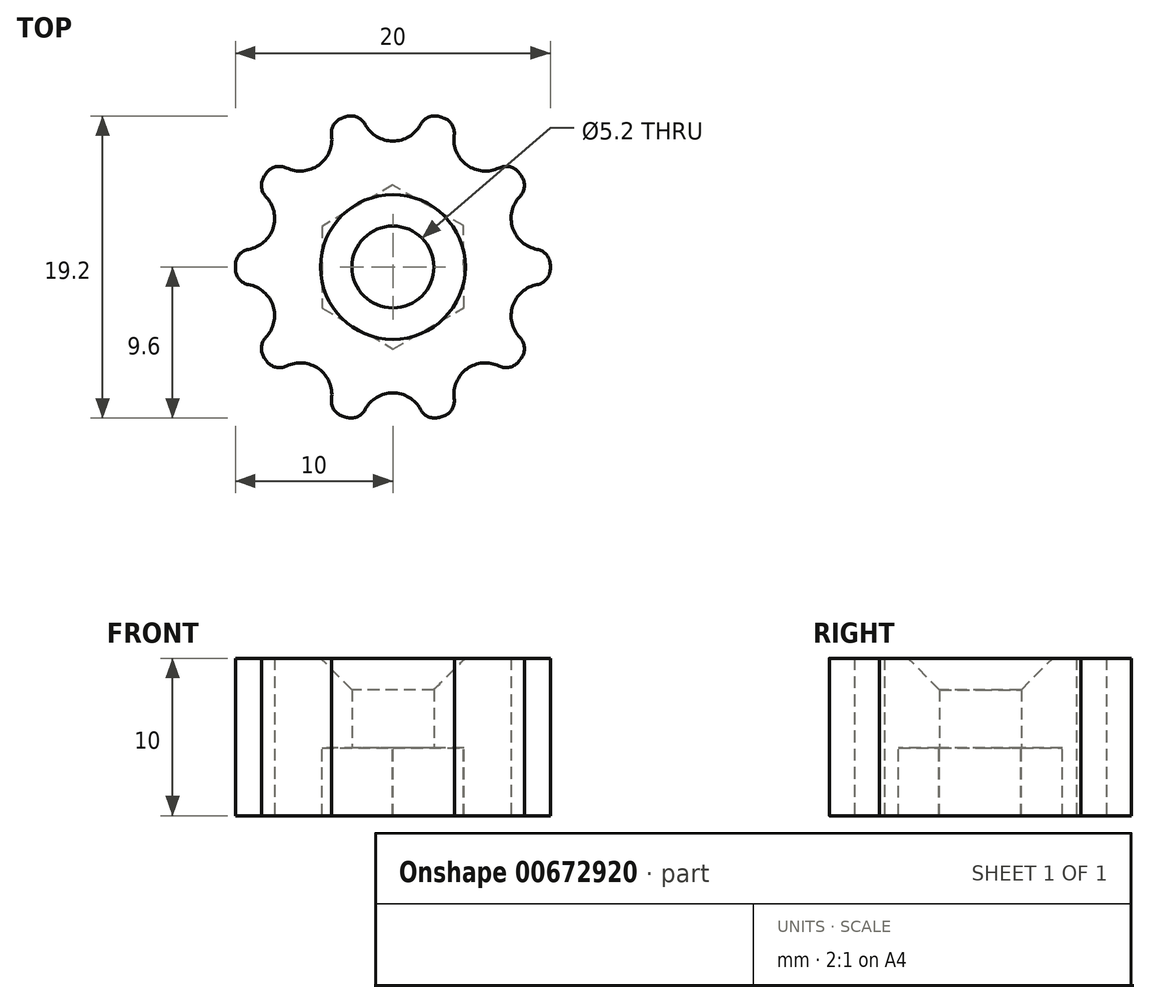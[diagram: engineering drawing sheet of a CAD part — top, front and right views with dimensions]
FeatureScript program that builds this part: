
annotation { "Feature Type Name" : "Feature", "Feature Type Description" : "" }
export const myFeature = defineFeature(function(context is Context, id is Id, definition is map)
    precondition{}
    {
        {
            var Q0;
            Q0=qCreatedBy(makeId("Top.planeOp"),FACE);
            var sketch = newSketch(context, id + "F0", { "sketchPlane" : qUnion([Q0])});
            skCircle(sketch, "E0", {"center": v(0, 0) * mm, "radius": 10 * mm});
            skCircle(sketch, "E1", {"center": v(0, 10) * mm, "radius": 2 * mm});
            skCircle(sketch, "E2.1.0", {"center": v(-5.88, 8.1) * mm, "radius": 2 * mm});
            skCircle(sketch, "E2.2.0", {"center": v(-9.51, 3.1) * mm, "radius": 2 * mm});
            skCircle(sketch, "E2.3.0", {"center": v(-9.51, -3.1) * mm, "radius": 2 * mm});
            skCircle(sketch, "E2.4.0", {"center": v(-5.88, -8.1) * mm, "radius": 2 * mm});
            skCircle(sketch, "E2.5.0", {"center": v(0, -10) * mm, "radius": 2 * mm});
            skCircle(sketch, "E2.6.0", {"center": v(5.88, -8.1) * mm, "radius": 2 * mm});
            skCircle(sketch, "E2.7.0", {"center": v(9.51, -3.1) * mm, "radius": 2 * mm});
            skCircle(sketch, "E2.8.0", {"center": v(9.51, 3.1) * mm, "radius": 2 * mm});
            skCircle(sketch, "E2.9.0", {"center": v(5.88, 8.1) * mm, "radius": 2 * mm});
            skCircle(sketch, "E3", {"center": v(0, 0) * mm, "radius": 2.6 * mm});
            skSolve(sketch);
        }
        {
            var Q0;
            {var subQ0=sQuery(id+"F0.wireOp",EDGE,"E2.8.0");var subQ1=sQuery(id+"F0.wireOp",EDGE,"E0");var subQ17=makeQuery(id+"F0.imprint","INTERSECT",VERTEX,{"disambiguationData":[OD(0.0)],"derivedFrom":[subQ1,subQ0]});Q0=makeQuery(id+"F0.imprint","IMPRINT",FACE,{"disambiguationData":[TD([[makeQuery(id+"F0.imprint","IMPRINT",EDGE,{"disambiguationData":[TD([[subQ17,-1.0]])],"derivedFrom":subQ1}),1.0]])]});}
            extrude(context, id + "F1", {"entities" : qUnion([Q0]), "depth" : 5.7 * mm, "offsetDistance" : 25 * mm});
        }
        {
            var Q0;
            Q0=makeQuery(id+"F1.opExtrude","CAP_EDGE",EDGE,{"disambiguationData":[OSD([sQuery(id+"F0.wireOp",EDGE,"E3")])],"isStart":false});
            chamfer(context, id + "F2", {"entities" : qUnion([Q0]), "width" : 2 * mm, "tangentPropagation" : true});
        }
        {
            var Q0;
            Q0=makeQuery(id+"F1.opExtrude","CAP_FACE",FACE,{"disambiguationData":[OSD([sQuery(id+"F0.wireOp",EDGE,"E0"),sQuery(id+"F0.wireOp",EDGE,"E1"),sQuery(id+"F0.wireOp",EDGE,"E2.1.0"),sQuery(id+"F0.wireOp",EDGE,"E2.2.0"),sQuery(id+"F0.wireOp",EDGE,"E2.3.0"),sQuery(id+"F0.wireOp",EDGE,"E2.4.0"),sQuery(id+"F0.wireOp",EDGE,"E2.5.0"),sQuery(id+"F0.wireOp",EDGE,"E2.6.0"),sQuery(id+"F0.wireOp",EDGE,"E2.7.0"),sQuery(id+"F0.wireOp",EDGE,"E2.8.0"),sQuery(id+"F0.wireOp",EDGE,"E2.9.0"),sQuery(id+"F0.wireOp",EDGE,"E3")])],"isStart":true});
            var sketch = newSketch(context, id + "F3", { "sketchPlane" : qUnion([Q0])});
            skCircle(sketch, "E4.cCircle", {"center": v(0, 0) * mm, "radius": 4.5 * mm, "construction": true});
            skLineSegment(sketch, "E4.0", {"start": v(-4.5, 2.62) * mm, "end": v(0.02, 5.2) * mm});
            skLineSegment(sketch, "E4.1", {"start": v(0.02, 5.2) * mm, "end": v(4.51, 2.58) * mm});
            skLineSegment(sketch, "E4.2", {"start": v(4.51, 2.58) * mm, "end": v(4.5, -2.62) * mm});
            skLineSegment(sketch, "E4.3", {"start": v(4.5, -2.62) * mm, "end": v(-0.02, -5.2) * mm});
            skLineSegment(sketch, "E4.4", {"start": v(-0.02, -5.2) * mm, "end": v(-4.51, -2.58) * mm});
            skLineSegment(sketch, "E4.5", {"start": v(-4.51, -2.58) * mm, "end": v(-4.5, 2.62) * mm});
            skPoint(sketch, "E4.0.midPoint", {"position": v(-2.24, 3.9) * mm});
            skSolve(sketch);
        }
        {
            var Q0;
            Q0=makeQuery(id+"F3.imprint","IMPRINT",FACE,{"disambiguationData":[TD([[makeQuery(id+"F3.imprint","IMPRINT",EDGE,{"derivedFrom":sQuery(id+"F3.wireOp",EDGE,"E4.0")}),1.0]])]});
            extrude(context, id + "F4", {"entities" : qUnion([Q0]), "operationType" : NewBodyOperationType.ADD, "depth" : 4.3 * mm, "offsetDistance" : 25 * mm});
        }
        {
            var Q0;
            {var subQ0=sQuery(id+"F0.wireOp",EDGE,"E2.7.0");var subQ1=sQuery(id+"F0.wireOp",EDGE,"E0");var subQ2=makeQuery(id+"F0.imprint","INTERSECT",VERTEX,{"disambiguationData":[OD(0.0)],"derivedFrom":[subQ1,subQ0]});Q0=makeQuery(id+"F4.boolean.opBoolean","MERGE",EDGE,{"derivedFrom":[makeQuery(id+"F1.opExtrude","SWEPT_EDGE",EDGE,{"disambiguationData":[OSD([subQ1,subQ0]),TDD([subQ2])]}),makeQuery(id+"F4.opExtrude","SWEPT_EDGE",EDGE,{"disambiguationData":[OSD([subQ1,subQ0]),TDD([makeQuery(id+"F3.imprint","INTERSECT",VERTEX,{"derivedFrom":[makeQuery(id+"F1.opExtrude","CAP_EDGE",EDGE,{"disambiguationData":[OSD([subQ1]),TDD([makeQuery(id+"F0.imprint","IMPRINT",EDGE,{"disambiguationData":[TD([[makeQuery(id+"F0.imprint","INTERSECT",VERTEX,{"disambiguationData":[OD(1.0)],"derivedFrom":[subQ1,sQuery(id+"F0.wireOp",EDGE,"E2.6.0")]}),-1.0]])],"derivedFrom":subQ1})])],"isStart":true}),makeQuery(id+"F1.opExtrude","CAP_EDGE",EDGE,{"disambiguationData":[OSD([subQ0])],"isStart":true})]})])]})]});}
            var Q1;
            {var subQ0=sQuery(id+"F0.wireOp",EDGE,"E2.6.0");var subQ1=sQuery(id+"F0.wireOp",EDGE,"E0");var subQ2=makeQuery(id+"F0.imprint","INTERSECT",VERTEX,{"disambiguationData":[OD(1.0)],"derivedFrom":[subQ1,subQ0]});Q1=makeQuery(id+"F4.boolean.opBoolean","MERGE",EDGE,{"derivedFrom":[makeQuery(id+"F1.opExtrude","SWEPT_EDGE",EDGE,{"disambiguationData":[OSD([subQ1,subQ0]),TDD([subQ2])]}),makeQuery(id+"F4.opExtrude","SWEPT_EDGE",EDGE,{"disambiguationData":[OSD([subQ1,subQ0]),TDD([makeQuery(id+"F3.imprint","INTERSECT",VERTEX,{"derivedFrom":[makeQuery(id+"F1.opExtrude","CAP_EDGE",EDGE,{"disambiguationData":[OSD([subQ1]),TDD([makeQuery(id+"F0.imprint","IMPRINT",EDGE,{"disambiguationData":[TD([[subQ2,-1.0]])],"derivedFrom":subQ1})])],"isStart":true}),makeQuery(id+"F1.opExtrude","CAP_EDGE",EDGE,{"disambiguationData":[OSD([subQ0])],"isStart":true})]})])]})]});}
            var Q2;
            {var subQ0=sQuery(id+"F0.wireOp",EDGE,"E2.6.0");var subQ1=sQuery(id+"F0.wireOp",EDGE,"E0");var subQ2=makeQuery(id+"F0.imprint","INTERSECT",VERTEX,{"disambiguationData":[OD(0.0)],"derivedFrom":[subQ1,subQ0]});Q2=makeQuery(id+"F4.boolean.opBoolean","MERGE",EDGE,{"derivedFrom":[makeQuery(id+"F1.opExtrude","SWEPT_EDGE",EDGE,{"disambiguationData":[OSD([subQ1,subQ0]),TDD([subQ2])]}),makeQuery(id+"F4.opExtrude","SWEPT_EDGE",EDGE,{"disambiguationData":[OSD([subQ1,subQ0]),TDD([makeQuery(id+"F3.imprint","INTERSECT",VERTEX,{"derivedFrom":[makeQuery(id+"F1.opExtrude","CAP_EDGE",EDGE,{"disambiguationData":[OSD([subQ1]),TDD([makeQuery(id+"F0.imprint","IMPRINT",EDGE,{"disambiguationData":[TD([[makeQuery(id+"F0.imprint","INTERSECT",VERTEX,{"disambiguationData":[OD(1.0)],"derivedFrom":[subQ1,sQuery(id+"F0.wireOp",EDGE,"E2.5.0")]}),-1.0]])],"derivedFrom":subQ1})])],"isStart":true}),makeQuery(id+"F1.opExtrude","CAP_EDGE",EDGE,{"disambiguationData":[OSD([subQ0])],"isStart":true})]})])]})]});}
            var Q3;
            {var subQ0=sQuery(id+"F0.wireOp",EDGE,"E2.5.0");var subQ1=sQuery(id+"F0.wireOp",EDGE,"E0");var subQ2=makeQuery(id+"F0.imprint","INTERSECT",VERTEX,{"disambiguationData":[OD(1.0)],"derivedFrom":[subQ1,subQ0]});Q3=makeQuery(id+"F4.boolean.opBoolean","MERGE",EDGE,{"derivedFrom":[makeQuery(id+"F1.opExtrude","SWEPT_EDGE",EDGE,{"disambiguationData":[OSD([subQ1,subQ0]),TDD([subQ2])]}),makeQuery(id+"F4.opExtrude","SWEPT_EDGE",EDGE,{"disambiguationData":[OSD([subQ1,subQ0]),TDD([makeQuery(id+"F3.imprint","INTERSECT",VERTEX,{"derivedFrom":[makeQuery(id+"F1.opExtrude","CAP_EDGE",EDGE,{"disambiguationData":[OSD([subQ1]),TDD([makeQuery(id+"F0.imprint","IMPRINT",EDGE,{"disambiguationData":[TD([[subQ2,-1.0]])],"derivedFrom":subQ1})])],"isStart":true}),makeQuery(id+"F1.opExtrude","CAP_EDGE",EDGE,{"disambiguationData":[OSD([subQ0])],"isStart":true})]})])]})]});}
            var Q4;
            {var subQ0=sQuery(id+"F0.wireOp",EDGE,"E2.5.0");var subQ1=sQuery(id+"F0.wireOp",EDGE,"E0");var subQ2=makeQuery(id+"F0.imprint","INTERSECT",VERTEX,{"disambiguationData":[OD(0.0)],"derivedFrom":[subQ1,subQ0]});Q4=makeQuery(id+"F4.boolean.opBoolean","MERGE",EDGE,{"derivedFrom":[makeQuery(id+"F1.opExtrude","SWEPT_EDGE",EDGE,{"disambiguationData":[OSD([subQ1,subQ0]),TDD([subQ2])]}),makeQuery(id+"F4.opExtrude","SWEPT_EDGE",EDGE,{"disambiguationData":[OSD([subQ1,subQ0]),TDD([makeQuery(id+"F3.imprint","INTERSECT",VERTEX,{"derivedFrom":[makeQuery(id+"F1.opExtrude","CAP_EDGE",EDGE,{"disambiguationData":[OSD([subQ1]),TDD([makeQuery(id+"F0.imprint","IMPRINT",EDGE,{"disambiguationData":[TD([[makeQuery(id+"F0.imprint","INTERSECT",VERTEX,{"disambiguationData":[OD(1.0)],"derivedFrom":[subQ1,sQuery(id+"F0.wireOp",EDGE,"E2.4.0")]}),-1.0]])],"derivedFrom":subQ1})])],"isStart":true}),makeQuery(id+"F1.opExtrude","CAP_EDGE",EDGE,{"disambiguationData":[OSD([subQ0])],"isStart":true})]})])]})]});}
            var Q5;
            {var subQ0=sQuery(id+"F0.wireOp",EDGE,"E2.4.0");var subQ1=sQuery(id+"F0.wireOp",EDGE,"E0");var subQ2=makeQuery(id+"F0.imprint","INTERSECT",VERTEX,{"disambiguationData":[OD(1.0)],"derivedFrom":[subQ1,subQ0]});Q5=makeQuery(id+"F4.boolean.opBoolean","MERGE",EDGE,{"derivedFrom":[makeQuery(id+"F1.opExtrude","SWEPT_EDGE",EDGE,{"disambiguationData":[OSD([subQ1,subQ0]),TDD([subQ2])]}),makeQuery(id+"F4.opExtrude","SWEPT_EDGE",EDGE,{"disambiguationData":[OSD([subQ1,subQ0]),TDD([makeQuery(id+"F3.imprint","INTERSECT",VERTEX,{"derivedFrom":[makeQuery(id+"F1.opExtrude","CAP_EDGE",EDGE,{"disambiguationData":[OSD([subQ1]),TDD([makeQuery(id+"F0.imprint","IMPRINT",EDGE,{"disambiguationData":[TD([[subQ2,-1.0]])],"derivedFrom":subQ1})])],"isStart":true}),makeQuery(id+"F1.opExtrude","CAP_EDGE",EDGE,{"disambiguationData":[OSD([subQ0])],"isStart":true})]})])]})]});}
            var Q6;
            {var subQ0=sQuery(id+"F0.wireOp",EDGE,"E2.4.0");var subQ1=sQuery(id+"F0.wireOp",EDGE,"E0");var subQ2=makeQuery(id+"F0.imprint","INTERSECT",VERTEX,{"disambiguationData":[OD(0.0)],"derivedFrom":[subQ1,subQ0]});Q6=makeQuery(id+"F4.boolean.opBoolean","MERGE",EDGE,{"derivedFrom":[makeQuery(id+"F1.opExtrude","SWEPT_EDGE",EDGE,{"disambiguationData":[OSD([subQ1,subQ0]),TDD([subQ2])]}),makeQuery(id+"F4.opExtrude","SWEPT_EDGE",EDGE,{"disambiguationData":[OSD([subQ1,subQ0]),TDD([makeQuery(id+"F3.imprint","INTERSECT",VERTEX,{"derivedFrom":[makeQuery(id+"F1.opExtrude","CAP_EDGE",EDGE,{"disambiguationData":[OSD([subQ1]),TDD([makeQuery(id+"F0.imprint","IMPRINT",EDGE,{"disambiguationData":[TD([[makeQuery(id+"F0.imprint","INTERSECT",VERTEX,{"disambiguationData":[OD(1.0)],"derivedFrom":[subQ1,sQuery(id+"F0.wireOp",EDGE,"E2.3.0")]}),-1.0]])],"derivedFrom":subQ1})])],"isStart":true}),makeQuery(id+"F1.opExtrude","CAP_EDGE",EDGE,{"disambiguationData":[OSD([subQ0])],"isStart":true})]})])]})]});}
            var Q7;
            {var subQ0=sQuery(id+"F0.wireOp",EDGE,"E2.3.0");var subQ1=sQuery(id+"F0.wireOp",EDGE,"E0");var subQ2=makeQuery(id+"F0.imprint","INTERSECT",VERTEX,{"disambiguationData":[OD(1.0)],"derivedFrom":[subQ1,subQ0]});Q7=makeQuery(id+"F4.boolean.opBoolean","MERGE",EDGE,{"derivedFrom":[makeQuery(id+"F1.opExtrude","SWEPT_EDGE",EDGE,{"disambiguationData":[OSD([subQ1,subQ0]),TDD([subQ2])]}),makeQuery(id+"F4.opExtrude","SWEPT_EDGE",EDGE,{"disambiguationData":[OSD([subQ1,subQ0]),TDD([makeQuery(id+"F3.imprint","INTERSECT",VERTEX,{"derivedFrom":[makeQuery(id+"F1.opExtrude","CAP_EDGE",EDGE,{"disambiguationData":[OSD([subQ1]),TDD([makeQuery(id+"F0.imprint","IMPRINT",EDGE,{"disambiguationData":[TD([[subQ2,-1.0]])],"derivedFrom":subQ1})])],"isStart":true}),makeQuery(id+"F1.opExtrude","CAP_EDGE",EDGE,{"disambiguationData":[OSD([subQ0])],"isStart":true})]})])]})]});}
            var Q8;
            {var subQ0=sQuery(id+"F0.wireOp",EDGE,"E2.3.0");var subQ1=sQuery(id+"F0.wireOp",EDGE,"E0");var subQ2=makeQuery(id+"F0.imprint","INTERSECT",VERTEX,{"disambiguationData":[OD(0.0)],"derivedFrom":[subQ1,subQ0]});Q8=makeQuery(id+"F4.boolean.opBoolean","MERGE",EDGE,{"derivedFrom":[makeQuery(id+"F1.opExtrude","SWEPT_EDGE",EDGE,{"disambiguationData":[OSD([subQ1,subQ0]),TDD([subQ2])]}),makeQuery(id+"F4.opExtrude","SWEPT_EDGE",EDGE,{"disambiguationData":[OSD([subQ1,subQ0]),TDD([makeQuery(id+"F3.imprint","INTERSECT",VERTEX,{"derivedFrom":[makeQuery(id+"F1.opExtrude","CAP_EDGE",EDGE,{"disambiguationData":[OSD([subQ1]),TDD([makeQuery(id+"F0.imprint","IMPRINT",EDGE,{"disambiguationData":[TD([[makeQuery(id+"F0.imprint","INTERSECT",VERTEX,{"disambiguationData":[OD(1.0)],"derivedFrom":[subQ1,sQuery(id+"F0.wireOp",EDGE,"E2.2.0")]}),-1.0]])],"derivedFrom":subQ1})])],"isStart":true}),makeQuery(id+"F1.opExtrude","CAP_EDGE",EDGE,{"disambiguationData":[OSD([subQ0])],"isStart":true})]})])]})]});}
            var Q9;
            {var subQ0=sQuery(id+"F0.wireOp",EDGE,"E2.2.0");var subQ1=sQuery(id+"F0.wireOp",EDGE,"E0");var subQ2=makeQuery(id+"F0.imprint","INTERSECT",VERTEX,{"disambiguationData":[OD(1.0)],"derivedFrom":[subQ1,subQ0]});Q9=makeQuery(id+"F4.boolean.opBoolean","MERGE",EDGE,{"derivedFrom":[makeQuery(id+"F1.opExtrude","SWEPT_EDGE",EDGE,{"disambiguationData":[OSD([subQ1,subQ0]),TDD([subQ2])]}),makeQuery(id+"F4.opExtrude","SWEPT_EDGE",EDGE,{"disambiguationData":[OSD([subQ1,subQ0]),TDD([makeQuery(id+"F3.imprint","INTERSECT",VERTEX,{"derivedFrom":[makeQuery(id+"F1.opExtrude","CAP_EDGE",EDGE,{"disambiguationData":[OSD([subQ1]),TDD([makeQuery(id+"F0.imprint","IMPRINT",EDGE,{"disambiguationData":[TD([[subQ2,-1.0]])],"derivedFrom":subQ1})])],"isStart":true}),makeQuery(id+"F1.opExtrude","CAP_EDGE",EDGE,{"disambiguationData":[OSD([subQ0])],"isStart":true})]})])]})]});}
            var Q10;
            {var subQ0=sQuery(id+"F0.wireOp",EDGE,"E2.2.0");var subQ1=sQuery(id+"F0.wireOp",EDGE,"E0");var subQ2=makeQuery(id+"F0.imprint","INTERSECT",VERTEX,{"disambiguationData":[OD(0.0)],"derivedFrom":[subQ1,subQ0]});Q10=makeQuery(id+"F4.boolean.opBoolean","MERGE",EDGE,{"derivedFrom":[makeQuery(id+"F1.opExtrude","SWEPT_EDGE",EDGE,{"disambiguationData":[OSD([subQ1,subQ0]),TDD([subQ2])]}),makeQuery(id+"F4.opExtrude","SWEPT_EDGE",EDGE,{"disambiguationData":[OSD([subQ1,subQ0]),TDD([makeQuery(id+"F3.imprint","INTERSECT",VERTEX,{"derivedFrom":[makeQuery(id+"F1.opExtrude","CAP_EDGE",EDGE,{"disambiguationData":[OSD([subQ1]),TDD([makeQuery(id+"F0.imprint","IMPRINT",EDGE,{"disambiguationData":[TD([[makeQuery(id+"F0.imprint","INTERSECT",VERTEX,{"disambiguationData":[OD(1.0)],"derivedFrom":[subQ1,sQuery(id+"F0.wireOp",EDGE,"E2.1.0")]}),-1.0]])],"derivedFrom":subQ1})])],"isStart":true}),makeQuery(id+"F1.opExtrude","CAP_EDGE",EDGE,{"disambiguationData":[OSD([subQ0])],"isStart":true})]})])]})]});}
            var Q11;
            {var subQ0=sQuery(id+"F0.wireOp",EDGE,"E2.1.0");var subQ1=sQuery(id+"F0.wireOp",EDGE,"E0");var subQ2=makeQuery(id+"F0.imprint","INTERSECT",VERTEX,{"disambiguationData":[OD(1.0)],"derivedFrom":[subQ1,subQ0]});Q11=makeQuery(id+"F4.boolean.opBoolean","MERGE",EDGE,{"derivedFrom":[makeQuery(id+"F1.opExtrude","SWEPT_EDGE",EDGE,{"disambiguationData":[OSD([subQ1,subQ0]),TDD([subQ2])]}),makeQuery(id+"F4.opExtrude","SWEPT_EDGE",EDGE,{"disambiguationData":[OSD([subQ1,subQ0]),TDD([makeQuery(id+"F3.imprint","INTERSECT",VERTEX,{"derivedFrom":[makeQuery(id+"F1.opExtrude","CAP_EDGE",EDGE,{"disambiguationData":[OSD([subQ1]),TDD([makeQuery(id+"F0.imprint","IMPRINT",EDGE,{"disambiguationData":[TD([[subQ2,-1.0]])],"derivedFrom":subQ1})])],"isStart":true}),makeQuery(id+"F1.opExtrude","CAP_EDGE",EDGE,{"disambiguationData":[OSD([subQ0])],"isStart":true})]})])]})]});}
            var Q12;
            {var subQ0=sQuery(id+"F0.wireOp",EDGE,"E2.1.0");var subQ1=sQuery(id+"F0.wireOp",EDGE,"E0");var subQ2=makeQuery(id+"F0.imprint","INTERSECT",VERTEX,{"disambiguationData":[OD(0.0)],"derivedFrom":[subQ1,subQ0]});Q12=makeQuery(id+"F4.boolean.opBoolean","MERGE",EDGE,{"derivedFrom":[makeQuery(id+"F1.opExtrude","SWEPT_EDGE",EDGE,{"disambiguationData":[OSD([subQ1,subQ0]),TDD([subQ2])]}),makeQuery(id+"F4.opExtrude","SWEPT_EDGE",EDGE,{"disambiguationData":[OSD([subQ1,subQ0]),TDD([makeQuery(id+"F3.imprint","INTERSECT",VERTEX,{"derivedFrom":[makeQuery(id+"F1.opExtrude","CAP_EDGE",EDGE,{"disambiguationData":[OSD([subQ1]),TDD([makeQuery(id+"F0.imprint","IMPRINT",EDGE,{"disambiguationData":[TD([[makeQuery(id+"F0.imprint","INTERSECT",VERTEX,{"disambiguationData":[OD(1.0)],"derivedFrom":[subQ1,sQuery(id+"F0.wireOp",EDGE,"E1")]}),-1.0]])],"derivedFrom":subQ1})])],"isStart":true}),makeQuery(id+"F1.opExtrude","CAP_EDGE",EDGE,{"disambiguationData":[OSD([subQ0])],"isStart":true})]})])]})]});}
            var Q13;
            {var subQ0=sQuery(id+"F0.wireOp",EDGE,"E1");var subQ1=sQuery(id+"F0.wireOp",EDGE,"E0");var subQ2=makeQuery(id+"F0.imprint","INTERSECT",VERTEX,{"disambiguationData":[OD(1.0)],"derivedFrom":[subQ1,subQ0]});Q13=makeQuery(id+"F4.boolean.opBoolean","MERGE",EDGE,{"derivedFrom":[makeQuery(id+"F1.opExtrude","SWEPT_EDGE",EDGE,{"disambiguationData":[OSD([subQ1,subQ0]),TDD([subQ2])]}),makeQuery(id+"F4.opExtrude","SWEPT_EDGE",EDGE,{"disambiguationData":[OSD([subQ1,subQ0]),TDD([makeQuery(id+"F3.imprint","INTERSECT",VERTEX,{"derivedFrom":[makeQuery(id+"F1.opExtrude","CAP_EDGE",EDGE,{"disambiguationData":[OSD([subQ1]),TDD([makeQuery(id+"F0.imprint","IMPRINT",EDGE,{"disambiguationData":[TD([[subQ2,-1.0]])],"derivedFrom":subQ1})])],"isStart":true}),makeQuery(id+"F1.opExtrude","CAP_EDGE",EDGE,{"disambiguationData":[OSD([subQ0])],"isStart":true})]})])]})]});}
            var Q14;
            {var subQ0=sQuery(id+"F0.wireOp",EDGE,"E1");var subQ1=sQuery(id+"F0.wireOp",EDGE,"E0");var subQ2=makeQuery(id+"F0.imprint","INTERSECT",VERTEX,{"disambiguationData":[OD(0.0)],"derivedFrom":[subQ1,subQ0]});Q14=makeQuery(id+"F4.boolean.opBoolean","MERGE",EDGE,{"derivedFrom":[makeQuery(id+"F1.opExtrude","SWEPT_EDGE",EDGE,{"disambiguationData":[OSD([subQ1,subQ0]),TDD([subQ2])]}),makeQuery(id+"F4.opExtrude","SWEPT_EDGE",EDGE,{"disambiguationData":[OSD([subQ1,subQ0]),TDD([makeQuery(id+"F3.imprint","INTERSECT",VERTEX,{"derivedFrom":[makeQuery(id+"F1.opExtrude","CAP_EDGE",EDGE,{"disambiguationData":[OSD([subQ1]),TDD([makeQuery(id+"F0.imprint","IMPRINT",EDGE,{"disambiguationData":[TD([[makeQuery(id+"F0.imprint","INTERSECT",VERTEX,{"disambiguationData":[OD(1.0)],"derivedFrom":[subQ1,sQuery(id+"F0.wireOp",EDGE,"E2.9.0")]}),-1.0]])],"derivedFrom":subQ1})])],"isStart":true}),makeQuery(id+"F1.opExtrude","CAP_EDGE",EDGE,{"disambiguationData":[OSD([subQ0])],"isStart":true})]})])]})]});}
            var Q15;
            {var subQ0=sQuery(id+"F0.wireOp",EDGE,"E2.9.0");var subQ1=sQuery(id+"F0.wireOp",EDGE,"E0");var subQ2=makeQuery(id+"F0.imprint","INTERSECT",VERTEX,{"disambiguationData":[OD(1.0)],"derivedFrom":[subQ1,subQ0]});Q15=makeQuery(id+"F4.boolean.opBoolean","MERGE",EDGE,{"derivedFrom":[makeQuery(id+"F1.opExtrude","SWEPT_EDGE",EDGE,{"disambiguationData":[OSD([subQ1,subQ0]),TDD([subQ2])]}),makeQuery(id+"F4.opExtrude","SWEPT_EDGE",EDGE,{"disambiguationData":[OSD([subQ1,subQ0]),TDD([makeQuery(id+"F3.imprint","INTERSECT",VERTEX,{"derivedFrom":[makeQuery(id+"F1.opExtrude","CAP_EDGE",EDGE,{"disambiguationData":[OSD([subQ1]),TDD([makeQuery(id+"F0.imprint","IMPRINT",EDGE,{"disambiguationData":[TD([[subQ2,-1.0]])],"derivedFrom":subQ1})])],"isStart":true}),makeQuery(id+"F1.opExtrude","CAP_EDGE",EDGE,{"disambiguationData":[OSD([subQ0])],"isStart":true})]})])]})]});}
            var Q16;
            {var subQ0=sQuery(id+"F0.wireOp",EDGE,"E2.9.0");var subQ1=sQuery(id+"F0.wireOp",EDGE,"E0");var subQ2=makeQuery(id+"F0.imprint","INTERSECT",VERTEX,{"disambiguationData":[OD(0.0)],"derivedFrom":[subQ1,subQ0]});Q16=makeQuery(id+"F4.boolean.opBoolean","MERGE",EDGE,{"derivedFrom":[makeQuery(id+"F1.opExtrude","SWEPT_EDGE",EDGE,{"disambiguationData":[OSD([subQ1,subQ0]),TDD([subQ2])]}),makeQuery(id+"F4.opExtrude","SWEPT_EDGE",EDGE,{"disambiguationData":[OSD([subQ1,subQ0]),TDD([makeQuery(id+"F3.imprint","INTERSECT",VERTEX,{"derivedFrom":[makeQuery(id+"F1.opExtrude","CAP_EDGE",EDGE,{"disambiguationData":[OSD([subQ1]),TDD([makeQuery(id+"F0.imprint","IMPRINT",EDGE,{"disambiguationData":[TD([[makeQuery(id+"F0.imprint","INTERSECT",VERTEX,{"disambiguationData":[OD(0.0)],"derivedFrom":[subQ1,sQuery(id+"F0.wireOp",EDGE,"E2.8.0")]}),-1.0]])],"derivedFrom":subQ1})])],"isStart":true}),makeQuery(id+"F1.opExtrude","CAP_EDGE",EDGE,{"disambiguationData":[OSD([subQ0])],"isStart":true})]})])]})]});}
            var Q17;
            {var subQ0=sQuery(id+"F0.wireOp",EDGE,"E2.8.0");var subQ1=sQuery(id+"F0.wireOp",EDGE,"E0");var subQ2=makeQuery(id+"F0.imprint","INTERSECT",VERTEX,{"disambiguationData":[OD(0.0)],"derivedFrom":[subQ1,subQ0]});Q17=makeQuery(id+"F4.boolean.opBoolean","MERGE",EDGE,{"derivedFrom":[makeQuery(id+"F1.opExtrude","SWEPT_EDGE",EDGE,{"disambiguationData":[OSD([subQ1,subQ0]),TDD([subQ2])]}),makeQuery(id+"F4.opExtrude","SWEPT_EDGE",EDGE,{"disambiguationData":[OSD([subQ1,subQ0]),TDD([makeQuery(id+"F3.imprint","INTERSECT",VERTEX,{"derivedFrom":[makeQuery(id+"F1.opExtrude","CAP_EDGE",EDGE,{"disambiguationData":[OSD([subQ1]),TDD([makeQuery(id+"F0.imprint","IMPRINT",EDGE,{"disambiguationData":[TD([[subQ2,-1.0]])],"derivedFrom":subQ1})])],"isStart":true}),makeQuery(id+"F1.opExtrude","CAP_EDGE",EDGE,{"disambiguationData":[OSD([subQ0])],"isStart":true})]})])]})]});}
            var Q18;
            {var subQ0=sQuery(id+"F0.wireOp",EDGE,"E2.8.0");var subQ1=sQuery(id+"F0.wireOp",EDGE,"E0");var subQ2=makeQuery(id+"F0.imprint","INTERSECT",VERTEX,{"disambiguationData":[OD(1.0)],"derivedFrom":[subQ1,subQ0]});Q18=makeQuery(id+"F4.boolean.opBoolean","MERGE",EDGE,{"derivedFrom":[makeQuery(id+"F1.opExtrude","SWEPT_EDGE",EDGE,{"disambiguationData":[OSD([subQ1,subQ0]),TDD([subQ2])]}),makeQuery(id+"F4.opExtrude","SWEPT_EDGE",EDGE,{"disambiguationData":[OSD([subQ1,subQ0]),TDD([makeQuery(id+"F3.imprint","INTERSECT",VERTEX,{"derivedFrom":[makeQuery(id+"F1.opExtrude","CAP_EDGE",EDGE,{"disambiguationData":[OSD([subQ1]),TDD([makeQuery(id+"F0.imprint","IMPRINT",EDGE,{"disambiguationData":[TD([[subQ2,1.0]])],"derivedFrom":subQ1})])],"isStart":true}),makeQuery(id+"F1.opExtrude","CAP_EDGE",EDGE,{"disambiguationData":[OSD([subQ0])],"isStart":true})]})])]})]});}
            var Q19;
            {var subQ0=sQuery(id+"F0.wireOp",EDGE,"E2.7.0");var subQ1=sQuery(id+"F0.wireOp",EDGE,"E0");var subQ2=makeQuery(id+"F0.imprint","INTERSECT",VERTEX,{"disambiguationData":[OD(1.0)],"derivedFrom":[subQ1,subQ0]});Q19=makeQuery(id+"F4.boolean.opBoolean","MERGE",EDGE,{"derivedFrom":[makeQuery(id+"F1.opExtrude","SWEPT_EDGE",EDGE,{"disambiguationData":[OSD([subQ1,subQ0]),TDD([subQ2])]}),makeQuery(id+"F4.opExtrude","SWEPT_EDGE",EDGE,{"disambiguationData":[OSD([subQ1,subQ0]),TDD([makeQuery(id+"F3.imprint","INTERSECT",VERTEX,{"derivedFrom":[makeQuery(id+"F1.opExtrude","CAP_EDGE",EDGE,{"disambiguationData":[OSD([subQ1]),TDD([makeQuery(id+"F0.imprint","IMPRINT",EDGE,{"disambiguationData":[TD([[makeQuery(id+"F0.imprint","INTERSECT",VERTEX,{"disambiguationData":[OD(1.0)],"derivedFrom":[subQ1,sQuery(id+"F0.wireOp",EDGE,"E2.8.0")]}),1.0]])],"derivedFrom":subQ1})])],"isStart":true}),makeQuery(id+"F1.opExtrude","CAP_EDGE",EDGE,{"disambiguationData":[OSD([subQ0])],"isStart":true})]})])]})]});}
            fillet(context, id + "F5", {"entities" : qUnion([Q0, Q1, Q2, Q3, Q4, Q5, Q6, Q7, Q8, Q9, Q10, Q11, Q12, Q13, Q14, Q15, Q16, Q17, Q18, Q19]), "radius" : 1.02 * mm, "tangentPropagation" : true, "allowEdgeOverflow" : false});
        }
    });
